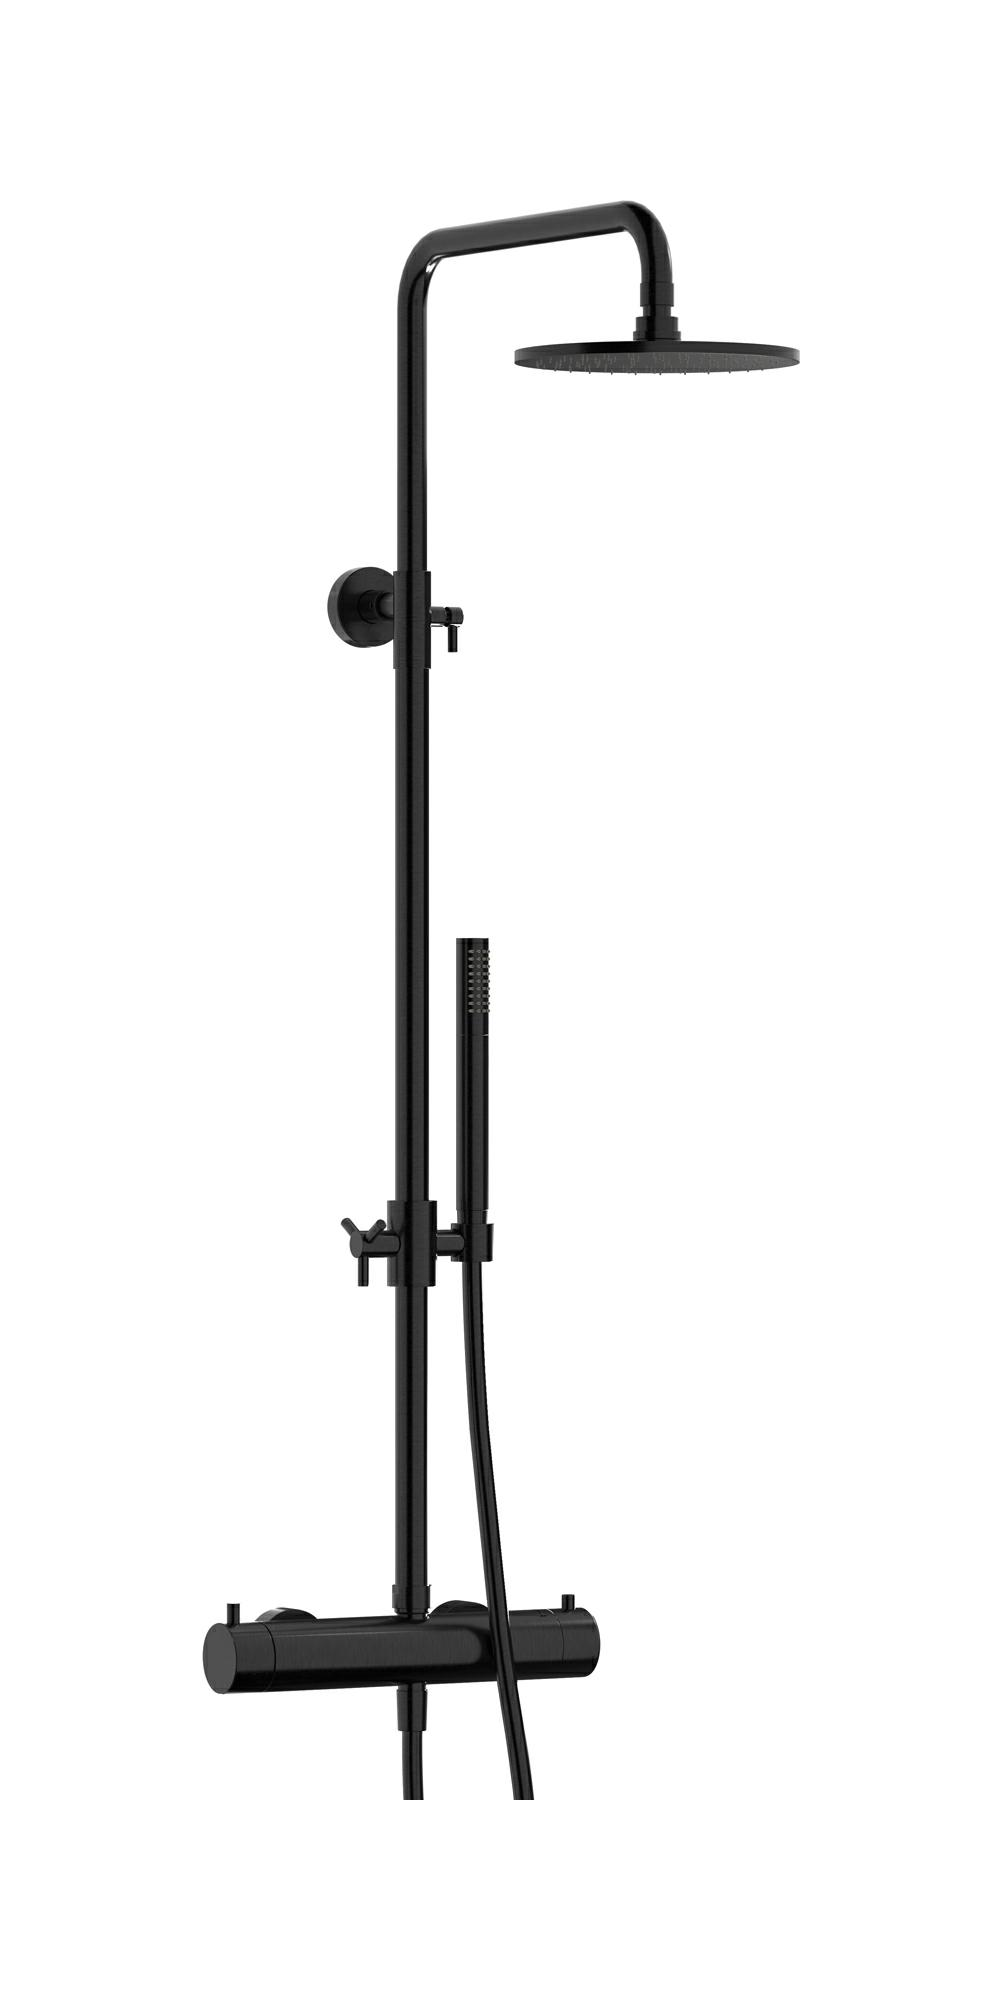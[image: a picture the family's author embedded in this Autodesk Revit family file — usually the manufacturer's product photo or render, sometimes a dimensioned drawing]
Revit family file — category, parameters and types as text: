
# Revit family: MT801
name_source: partatom
category: Apparecchi idraulici
units: mm (PartAtom-declared; Revit-internal decimal feet)

## family parameters
Basato su piano di lavoro = No
Condiviso = No
Mantieni orientamento annotazione = No
Numero OmniClass = 23.45.55.17
Punto di calcolo locali = No
Quota connettore circolare = Usa diametro
Sempre verticale = Sì
Taglio con vuoti quando caricato = No
Tipo di parte = Normale
Titolo OmniClass = Mixing Faucets

## types (12) — shared parameters
Cold water inlet = 10 mm  [stored 0.0328084 ft]
Commenti sul tipo = Thermostatic shower column with shower kit
Connessione CW = No
Connessione HW = No
Connessione di scarico = No
Connessione di ventilazione = No
Descrizione = Thermostatic shower column with shower kit
Hot water inlet = 10 mm  [stored 0.0328084 ft]
Produttore = IB Rubinetterie S.p.A.
URL = https://www.weareib.it
zero-valued in all types: Prospetto di default

## per-type parameters (varying)
| type | Finishes surface | Immagine tipo | Modello |
| Chrome | IB_Chrome | MT801CC.jpg | MT801CC |
| Brushed nickel | IB_Brushed nickel | MT801CC.jpg | MT801CC |
| Matt black | IB_matt black | MT801NP.jpg | MT801NP |
| Matt white | IB_matt white | MT801BO.jpg | MT801BO |
| Black chrome | IB_Black chrome | MT801CF copia.jpg | MT801CF |
| Brushed black chrome | IB_Brushed black chrome | MT801CS copia.jpg | MT801CS |
| Pale gold | IB_Pale gold | MT801II copia.jpg | MT801II |
| Brushed pale gold | IB_brushed pale gold | MT801IS copia.jpg | MT801IS |
| Rose gold | IB_Rose gold | MT801RS copia.jpg | MT801RS |
| Brushed rose gold | IB_Brushed rose gold | MT801SR copia.jpg | MT801SR |
| Gold | IB_gold | MT801OO copia.jpg | MT801OO |
| Brushed gold | IB_brushed gold | MT801OS copia.jpg | MT801OS |

note: [stored X ft] marks values corroborated as IEEE doubles in the binary element streams (Revit-internal decimal feet)
